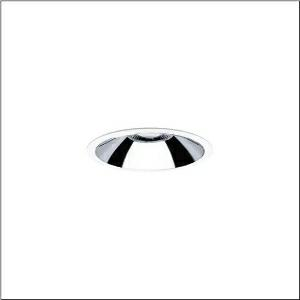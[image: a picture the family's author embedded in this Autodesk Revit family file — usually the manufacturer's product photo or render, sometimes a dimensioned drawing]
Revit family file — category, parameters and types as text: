
# Revit family: lunis_21_l_51db15md4c
name_source: partatom
category: Lighting Fixtures
units: mm (PartAtom-declared; Revit-internal decimal feet)

## family parameters
Cut with Voids When Loaded = No
Host = Face
Light Source = No
Part Type = Normal
Room Calculation Point = No
Round Connector Dimension = Use Diameter
Shared = No

## types (1)
- --- (1 x LED, 1700 lm, 13.8 W, 4000K)
    Apparent Load = 14 VA
    CIE Flux Codes = 90 99 100 100 100
    Color Rendering = 80
    Color Temperature = 4000K
    Default Elevation = 1800 mm
    Description = Lunis 21,  L, downlight, of PC, light emission: direct distribution, LED rated luminous flux: 1.700lm, light colour: 840, control gear: ECG, with terminal, 3-pole, mains connection: 220..240V, AC, housing, round, of diecast aluminium, traffic white (RAL 9016), diameter: 162mm, protection rating (complete): IP20, insulation class (complete): insulation class II (safety insulation), certification: CE, impact resistance: IK02, packaging unit: 1 piece
    Height = 0 mm  [stored 0 ft]
    Lamp = 1 x LED
    Lamp Light Flux = 1700 lm
    Lamp Power = 13.8 W
    Lamp count = 1
    Length = 162 mm
    Luminous efficacy = 123 lm/W
    Manufacturer = Siteco
    ModVariant = No
    Model = 51DB15MD4C
    Mounting Place = Ceiling
    Mounting Type = Recessed
    Number of Poles = 1
    OnlyDefault = Yes
    Power Factor = 1
    Product Name = Lunis 21 L
    Product group = downlight | ceiling recessed
    ProductGroupID = 402
    Protection Class = Protection class II
    Protection Degree = IP 20
    RLX_Detail_Level = 1
    RlxData = <blob elided: 21885 chars, md5=7dc16513>
    Socket = socket
    Standby Power = 0 W
    System Light Flux = 1700 lm
    System Power = 14 W
    Type Comments = factory setting: luminous flux: 100 % | (ON | ON)
    Type Image = l_1006992.jpg
    URL = http://relux.com
    VarID = @adj_078321
    Voltage = 0 V
    Weight = 0.00 kg
    Width = 0 mm  [stored 0 ft]

note: [stored X ft] marks values corroborated as IEEE doubles in the binary element streams (Revit-internal decimal feet)

## geometry (parser evidence)
native form markers: Blend x4, Sweep x11
no freeform markers — native parametric forms only
